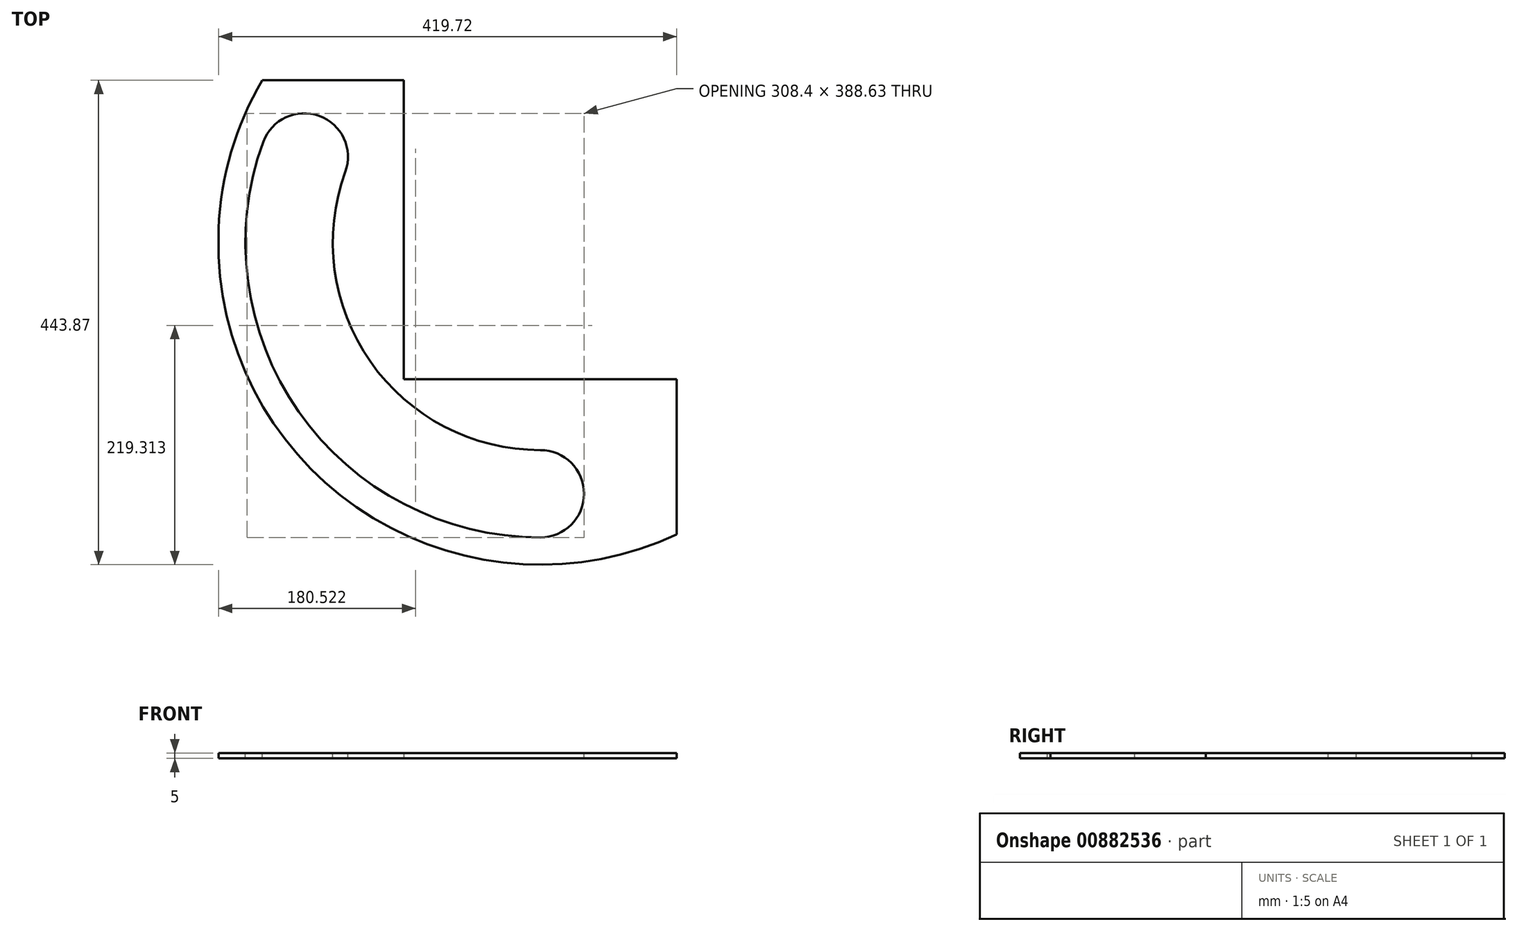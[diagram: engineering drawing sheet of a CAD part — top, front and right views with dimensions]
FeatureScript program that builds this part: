
annotation { "Feature Type Name" : "Feature", "Feature Type Description" : "" }
export const myFeature = defineFeature(function(context is Context, id is Id, definition is map)
    precondition{}
    {
        {
            var Q0;
            Q0=qCreatedBy(makeId("Top.planeOp"),FACE);
            var sketch = newSketch(context, id + "F0", { "sketchPlane" : qUnion([Q0])});
            skLineSegment(sketch, "E0.bottom", {"start": v(125, -125) * mm, "end": v(-125, -125) * mm});
            skLineSegment(sketch, "E0.top", {"start": v(125, 125) * mm, "end": v(-125, 125) * mm});
            skLineSegment(sketch, "E0.left", {"start": v(125, -125) * mm, "end": v(125, 125) * mm});
            skLineSegment(sketch, "E0.right", {"start": v(-125, -125) * mm, "end": v(-125, 125) * mm});
            skPoint(sketch, "E0.middle", {"position": v(0, 0) * mm});
            skLineSegment(sketch, "E1", {"start": v(0, 0) * mm, "end": v(-125, 0) * mm, "construction": true});
            skLineSegment(sketch, "E2.bottom", {"start": v(-349.96, 0) * mm, "end": v(0, 0) * mm});
            skLineSegment(sketch, "E2.left", {"start": v(-349.96, 0) * mm, "end": v(-349.96, 125) * mm});
            skLineSegment(sketch, "E2.right", {"start": v(125, 0) * mm, "end": v(125, 125) * mm});
            skLineSegment(sketch, "E3.MirrorCS", {"start": v(-349.96, 0) * mm, "end": v(-349.96, -249.62) * mm});
            skLineSegment(sketch, "E4.MirrorCS", {"start": v(-349.96, -249.62) * mm, "end": v(125, -249.62) * mm});
            skLineSegment(sketch, "E5.MirrorCS", {"start": v(125, 0) * mm, "end": v(125, -249.62) * mm});
            skLineSegment(sketch, "E6", {"start": v(-349.96, 125) * mm, "end": v(125, 125) * mm});
            skPoint(sketch, "E2.top.start.orphan", {"position": v(-349.96, 249.62) * mm});
            skPoint(sketch, "E7.orphan", {"position": v(125, 249.62) * mm});
            skLineSegment(sketch, "E8", {"start": v(-349.96, 29.15) * mm, "end": v(-125, 29.15) * mm});
            skLineSegment(sketch, "E9", {"start": v(-349.96, -249.62) * mm, "end": v(-349.96, -298.58) * mm});
            skLineSegment(sketch, "E10", {"start": v(-349.96, -298.58) * mm, "end": v(124.79, -298.58) * mm});
            skLineSegment(sketch, "E11", {"start": v(124.79, -298.58) * mm, "end": v(125, -249.62) * mm});
            skLineSegment(sketch, "E12", {"start": v(-294.72, 29.15) * mm, "end": v(-294.72, -298.58) * mm});
            skLineSegment(sketch, "E13", {"start": v(-294.72, 29.15) * mm, "end": v(-294.72, 125) * mm});
            skLineSegment(sketch, "E14", {"start": v(-294.72, 125) * mm, "end": v(-294.72, 148.87) * mm});
            skLineSegment(sketch, "E15", {"start": v(-294.72, 148.87) * mm, "end": v(-125.13, 148.87) * mm});
            skLineSegment(sketch, "E16", {"start": v(-125.13, 148.87) * mm, "end": v(-125, 125) * mm});
            skSolve(sketch);
        }
        {
            var Q0;
            {var subQ0=sQuery(id+"F0.wireOp",EDGE,"E8");var subQ1=sQuery(id+"F0.wireOp",EDGE,"E0.right");var subQ2=makeQuery(id+"F0.imprint","INTERSECT",VERTEX,{"derivedFrom":[subQ1,subQ0]});Q0=makeQuery(id+"F0.imprint","IMPRINT",FACE,{"disambiguationData":[TD([[makeQuery(id+"F0.imprint","IMPRINT",EDGE,{"disambiguationData":[TD([[subQ2,1.0]])],"derivedFrom":subQ1}),1.0]])]});}
            var Q1;
            {var subQ5=sQuery(id+"F0.wireOp",EDGE,"E0.bottom");Q1=makeQuery(id+"F0.imprint","IMPRINT",FACE,{"disambiguationData":[TD([[makeQuery(id+"F0.imprint","IMPRINT",EDGE,{"derivedFrom":subQ5}),1.0]])]});}
            var Q2;
            {var subQ0=sQuery(id+"F0.wireOp",EDGE,"E11");Q2=makeQuery(id+"F0.imprint","IMPRINT",FACE,{"disambiguationData":[TD([[makeQuery(id+"F0.imprint","IMPRINT",EDGE,{"derivedFrom":subQ0}),1.0]])]});}
            var Q3;
            {var subQ4=sQuery(id+"F0.wireOp",EDGE,"E6");var subQ5=sQuery(id+"F0.wireOp",EDGE,"E0.right");var subQ6=makeQuery(id+"F0.imprint","INTERSECT",VERTEX,{"derivedFrom":[subQ5,subQ4]});Q3=makeQuery(id+"F0.imprint","IMPRINT",FACE,{"disambiguationData":[TD([[makeQuery(id+"F0.imprint","IMPRINT",EDGE,{"disambiguationData":[TD([[subQ6,1.0]])],"derivedFrom":subQ5}),1.0]])]});}
            var Q4;
            {var subQ2=sQuery(id+"F0.wireOp",EDGE,"E14");Q4=makeQuery(id+"F0.imprint","IMPRINT",FACE,{"disambiguationData":[TD([[makeQuery(id+"F0.imprint","IMPRINT",EDGE,{"derivedFrom":subQ2}),-1.0]])]});}
            extrude(context, id + "F1", {"entities" : qUnion([Q0, Q1, Q2, Q3, Q4]), "depth" : 5 * mm, "offsetDistance" : 25 * mm});
        }
        {
            var Q0;
            Q0=makeQuery(id+"F1.opExtrude","CAP_FACE",FACE,{"disambiguationData":[OSD([sQuery(id+"F0.wireOp",EDGE,"E0.bottom"),sQuery(id+"F0.wireOp",EDGE,"E0.top"),sQuery(id+"F0.wireOp",EDGE,"E0.left"),sQuery(id+"F0.wireOp",EDGE,"E0.right"),sQuery(id+"F0.wireOp",EDGE,"E2.top"),sQuery(id+"F0.wireOp",EDGE,"E2.left"),sQuery(id+"F0.wireOp",EDGE,"E2.right"),sQuery(id+"F0.wireOp",EDGE,"E3.MirrorCS"),sQuery(id+"F0.wireOp",EDGE,"E4.MirrorCS"),sQuery(id+"F0.wireOp",EDGE,"E5.MirrorCS")])],"isStart":false});
            var sketch = newSketch(context, id + "F2", { "sketchPlane" : qUnion([Q0])});
            skCircle(sketch, "E17", {"center": v(0, 0) * mm, "radius": 270 * mm});
            skCircle(sketch, "E18", {"center": v(0, 0) * mm, "radius": 190 * mm});
            skLineSegment(sketch, "E19", {"start": v(0, 0) * mm, "end": v(-270, 0) * mm, "construction": true});
            skCircle(sketch, "E20", {"center": v(0, 0) * mm, "radius": 230 * mm, "construction": true});
            skCircle(sketch, "E21", {"center": v(-216.13, 78.66) * mm, "radius": 40 * mm});
            skCircle(sketch, "E22", {"center": v(0, -230) * mm, "radius": 40 * mm});
            skLineSegment(sketch, "E23", {"start": v(-216.13, 78.66) * mm, "end": v(0, 0) * mm, "construction": true});
            skLineSegment(sketch, "E24", {"start": v(0, 0) * mm, "end": v(0, -230) * mm, "construction": true});
            skSolve(sketch);
        }
        {
            var Q0;
            {var subQ0=sQuery(id+"F2.wireOp",EDGE,"E21");var subQ1=sQuery(id+"F2.wireOp",EDGE,"E17");var subQ2=makeQuery(id+"F2.imprint","INTERSECT",VERTEX,{"derivedFrom":[subQ1,subQ0]});Q0=makeQuery(id+"F2.imprint","IMPRINT",FACE,{"disambiguationData":[TD([[makeQuery(id+"F2.imprint","IMPRINT",EDGE,{"disambiguationData":[TD([[subQ2,-1.0]])],"derivedFrom":subQ1}),1.0]])]});}
            var Q1;
            {var subQ0=sQuery(id+"F2.wireOp",EDGE,"E21");var subQ1=makeQuery(id+"F2.imprint","INTERSECT",VERTEX,{"derivedFrom":[sQuery(id+"F2.wireOp",EDGE,"E17"),subQ0]});Q1=makeQuery(id+"F2.imprint","IMPRINT",FACE,{"disambiguationData":[TD([[makeQuery(id+"F2.imprint","IMPRINT",EDGE,{"disambiguationData":[TD([[subQ1,-1.0]])],"derivedFrom":subQ0}),1.0]])]});}
            var Q2;
            {var subQ0=sQuery(id+"F2.wireOp",EDGE,"E22");var subQ1=makeQuery(id+"F2.imprint","INTERSECT",VERTEX,{"derivedFrom":[sQuery(id+"F2.wireOp",EDGE,"E17"),subQ0]});Q2=makeQuery(id+"F2.imprint","IMPRINT",FACE,{"disambiguationData":[TD([[makeQuery(id+"F2.imprint","IMPRINT",EDGE,{"disambiguationData":[TD([[subQ1,1.0]])],"derivedFrom":subQ0}),1.0]])]});}
            var Q3;
            {var subQ0=sQuery(id+"F2.wireOp",EDGE,"E22");var subQ1=makeQuery(id+"F2.imprint","INTERSECT",VERTEX,{"derivedFrom":[sQuery(id+"F2.wireOp",EDGE,"E18"),subQ0]});Q3=makeQuery(id+"F2.imprint","IMPRINT",FACE,{"disambiguationData":[TD([[makeQuery(id+"F2.imprint","IMPRINT",EDGE,{"disambiguationData":[TD([[subQ1,-1.0]])],"derivedFrom":subQ0}),1.0]])]});}
            extrude(context, id + "F3", {"entities" : qUnion([Q0, Q1, Q2, Q3]), "operationType" : NewBodyOperationType.REMOVE, "oppositeDirection" : true, "depth" : 6 * mm, "offsetDistance" : 25 * mm});
        }
        {
            var Q0;
            Q0=makeQuery(id+"F1.opExtrude","CAP_FACE",FACE,{"disambiguationData":[OSD([sQuery(id+"F0.wireOp",EDGE,"E0.bottom"),sQuery(id+"F0.wireOp",EDGE,"E0.right"),sQuery(id+"F0.wireOp",EDGE,"E5.MirrorCS"),sQuery(id+"F0.wireOp",EDGE,"E8"),sQuery(id+"F0.wireOp",EDGE,"E10"),sQuery(id+"F0.wireOp",EDGE,"E11"),sQuery(id+"F0.wireOp",EDGE,"E12")])],"isStart":false});
            var sketch = newSketch(context, id + "F4", { "sketchPlane" : qUnion([Q0])});
            skCircle(sketch, "E25", {"center": v(0, 0) * mm, "radius": 295 * mm});
            skLineSegment(sketch, "E26", {"start": v(178.33, -235) * mm, "end": v(178.33, -361.67) * mm});
            skLineSegment(sketch, "E27", {"start": v(178.33, -361.67) * mm, "end": v(-429.48, -361.67) * mm});
            skLineSegment(sketch, "E28", {"start": v(-429.48, -361.67) * mm, "end": v(-429.48, 76.22) * mm});
            skLineSegment(sketch, "E29", {"start": v(-429.48, 76.22) * mm, "end": v(-284.98, 76.22) * mm});
            skSolve(sketch);
        }
        {
            var Q0;
            {var subQ0=sQuery(id+"F4.wireOp",EDGE,"E25");var subQ1=makeQuery(id+"F1.opExtrude","CAP_EDGE",EDGE,{"disambiguationData":[OSD([sQuery(id+"F0.wireOp",EDGE,"E12")])],"isStart":false});var subQ2=makeQuery(id+"F4.imprint","INTERSECT",VERTEX,{"disambiguationData":[OD(0.0)],"derivedFrom":[subQ1,subQ0]});Q0=makeQuery(id+"F4.imprint","IMPRINT",FACE,{"disambiguationData":[TD([[makeQuery(id+"F4.imprint","IMPRINT",EDGE,{"disambiguationData":[TD([[subQ2,-1.0]])],"derivedFrom":subQ0}),1.0]])]});}
            var Q1;
            {var subQ0=sQuery(id+"F4.wireOp",EDGE,"E25");var subQ1=makeQuery(id+"F1.opExtrude","CAP_EDGE",EDGE,{"disambiguationData":[OSD([sQuery(id+"F0.wireOp",EDGE,"E8")])],"isStart":false});var subQ2=makeQuery(id+"F4.imprint","INTERSECT",VERTEX,{"derivedFrom":[subQ1,subQ0]});Q1=makeQuery(id+"F4.imprint","IMPRINT",FACE,{"disambiguationData":[TD([[makeQuery(id+"F4.imprint","IMPRINT",EDGE,{"disambiguationData":[TD([[subQ2,-1.0]])],"derivedFrom":subQ0}),-1.0]])]});}
            var Q2;
            {var subQ11=sQuery(id+"F4.wireOp",EDGE,"E26");Q2=makeQuery(id+"F4.imprint","IMPRINT",FACE,{"disambiguationData":[TD([[makeQuery(id+"F4.imprint","IMPRINT",EDGE,{"derivedFrom":subQ11}),-1.0]])]});}
            var Q3;
            {var subQ5=makeQuery(id+"F1.opExtrude","CAP_EDGE",EDGE,{"disambiguationData":[OSD([sQuery(id+"F0.wireOp",EDGE,"E10")])],"isStart":false});Q3=makeQuery(id+"F4.imprint","IMPRINT",FACE,{"disambiguationData":[TD([[makeQuery(id+"F4.imprint","IMPRINT",EDGE,{"derivedFrom":subQ5}),1.0]])]});}
            var Q4;
            {var subQ0=sQuery(id+"F4.wireOp",EDGE,"E29");var subQ1=sQuery(id+"F4.wireOp",EDGE,"E25");var subQ2=makeQuery(id+"F4.imprint","INTERSECT",VERTEX,{"derivedFrom":[subQ1,subQ0]});Q4=makeQuery(id+"F4.imprint","IMPRINT",FACE,{"disambiguationData":[TD([[makeQuery(id+"F4.imprint","IMPRINT",EDGE,{"disambiguationData":[TD([[subQ2,-1.0]])],"derivedFrom":subQ1}),-1.0]])]});}
            var Q5;
            {var subQ0=sQuery(id+"F4.wireOp",EDGE,"E29");var subQ1=sQuery(id+"F4.wireOp",EDGE,"E25");var subQ2=makeQuery(id+"F4.imprint","INTERSECT",VERTEX,{"derivedFrom":[subQ1,subQ0]});Q5=makeQuery(id+"F4.imprint","IMPRINT",FACE,{"disambiguationData":[TD([[makeQuery(id+"F4.imprint","IMPRINT",EDGE,{"disambiguationData":[TD([[subQ2,1.0]])],"derivedFrom":subQ1}),-1.0]])]});}
            extrude(context, id + "F5", {"entities" : qUnion([Q0, Q1, Q2, Q3, Q4, Q5]), "operationType" : NewBodyOperationType.REMOVE, "oppositeDirection" : true, "depth" : 25 * mm, "offsetDistance" : 25 * mm});
        }
    });
